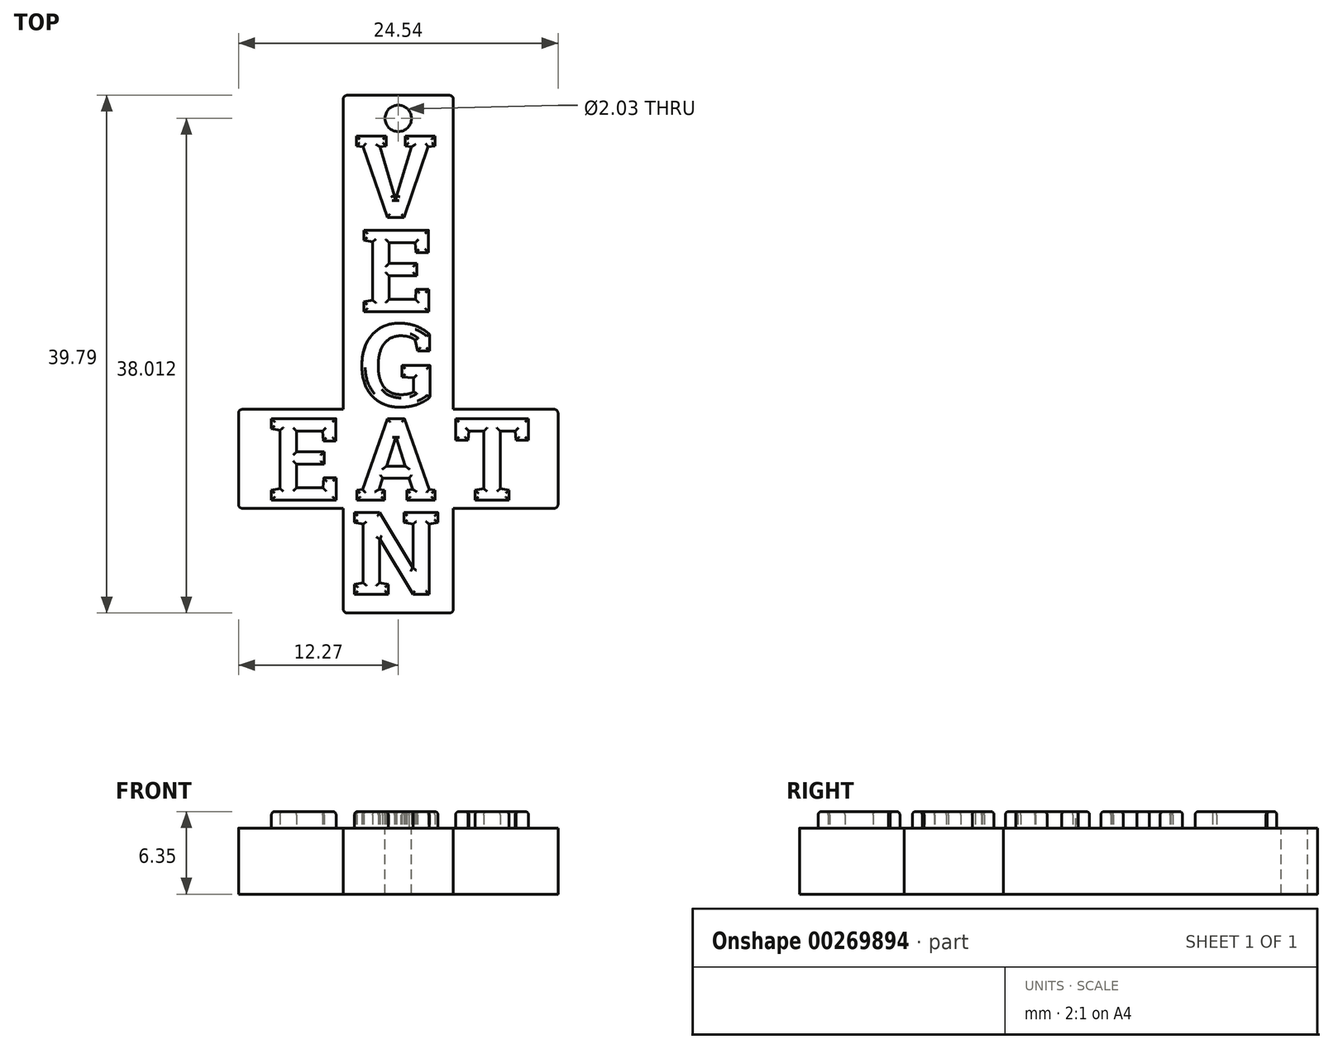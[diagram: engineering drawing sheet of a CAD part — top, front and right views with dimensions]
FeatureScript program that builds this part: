
annotation { "Feature Type Name" : "Feature", "Feature Type Description" : "" }
export const myFeature = defineFeature(function(context is Context, id is Id, definition is map)
    precondition{}
    {
        {
            var Q0;
            Q0=qCreatedBy(makeId("Top.planeOp"),FACE);
            cPlane(context, id + "F0", {"entities" : qUnion([Q0]), "cplaneType" : CPlaneType.OFFSET, "offset" : 5.08 * mm, "width" : 152.4 * mm, "height" : 152.4 * mm});
        }
        {
            var Q0;
            Q0=qCreatedBy(id+"F0.planeOp",FACE);
            var sketch = newSketch(context, id + "F1", { "sketchPlane" : qUnion([Q0])});
            skText(sketch, "E0", { "text": "G", "fontName": "RobotoSlab-Bold.ttf"});
            skText(sketch, "E1", { "text": "E", "fontName": "RobotoSlab-Bold.ttf"});
            skText(sketch, "E2", { "text": "V", "fontName": "RobotoSlab-Bold.ttf"});
            skText(sketch, "E3", { "text": "N", "fontName": "RobotoSlab-Bold.ttf"});
            skText(sketch, "E4", { "text": "A", "fontName": "RobotoSlab-Bold.ttf"});
            skText(sketch, "E5", { "text": "E", "fontName": "RobotoSlab-Bold.ttf"});
            skText(sketch, "E6", { "text": "T", "fontName": "RobotoSlab-Bold.ttf"});
            skPoint(sketch, "E7", {"position": v(-3.35, 0) * mm});
            skPoint(sketch, "E8", {"position": v(3.35, 0) * mm});
            skLineSegment(sketch, "E9", {"start": v(-3.35, 0) * mm, "end": v(3.35, 0) * mm, "construction": true});
            const initialGuessF1  = {"E0": [-0.00299, 0.00406, 1, 0, 0.00635], "E1": [-0.00287, 0.0113, 1, 0, 0.00635], "E2": [-0.00336, 0.01854, 1, 0, 0.00635], "E3": [-0.0036, -0.01041, 1, 0, 0.00635], "E4": [-0.00335, -0.00318, 1, 0, 0.00635], "E5": [-0.00998, -0.00318, 1, 0, 0.00635], "E6": [0.00424, -0.00318, 1, 0, 0.00635]};
            skSetInitialGuess(sketch, initialGuessF1);
            skSolve(sketch);
        }
        {
            var Q0;
            Q0=qCreatedBy(id+"F0.planeOp",FACE);
            var sketch = newSketch(context, id + "F2", { "sketchPlane" : qUnion([Q0])});
            skLineSegment(sketch, "E10.0", {"start": v(-3.6, -10.41) * mm, "end": v(-3.6, -4.06) * mm, "construction": true});
            skLineSegment(sketch, "E10.1", {"start": v(-3.6, -10.41) * mm, "end": v(3.6, -10.41) * mm, "construction": true});
            skLineSegment(sketch, "E10.2", {"start": v(3.6, -10.41) * mm, "end": v(3.6, -4.06) * mm, "construction": true});
            skLineSegment(sketch, "E10.3", {"start": v(-9.98, -3.18) * mm, "end": v(-9.98, 3.17) * mm, "construction": true});
            skLineSegment(sketch, "E10.4", {"start": v(-9.98, -3.18) * mm, "end": v(-4.24, -3.18) * mm, "construction": true});
            skLineSegment(sketch, "E10.5", {"start": v(-9.98, 3.17) * mm, "end": v(-4.24, 3.17) * mm, "construction": true});
            skLineSegment(sketch, "E10.6", {"start": v(4.24, 3.17) * mm, "end": v(10.54, 3.17) * mm, "construction": true});
            skLineSegment(sketch, "E10.7", {"start": v(10.54, -3.18) * mm, "end": v(10.54, 3.17) * mm, "construction": true});
            skLineSegment(sketch, "E10.8", {"start": v(4.24, -3.18) * mm, "end": v(10.54, -3.18) * mm, "construction": true});
            skLineSegment(sketch, "E11.0", {"start": v(-3.36, 18.54) * mm, "end": v(-3.36, 24.9) * mm, "construction": true});
            skLineSegment(sketch, "E11.1", {"start": v(-3.36, 24.9) * mm, "end": v(3.36, 24.9) * mm, "construction": true});
            skLineSegment(sketch, "E11.2", {"start": v(3.36, 18.54) * mm, "end": v(3.36, 24.9) * mm, "construction": true});
            skLineSegment(sketch, "E12.0", {"start": v(-4.23, -11.85) * mm, "end": v(-4.23, -3.81) * mm});
            skLineSegment(sketch, "E13.0", {"start": v(4.23, -11.85) * mm, "end": v(4.23, -3.81) * mm});
            skLineSegment(sketch, "E14.0", {"start": v(-12.27, 3.8) * mm, "end": v(-4.23, 3.8) * mm});
            skLineSegment(sketch, "E15.0", {"start": v(-12.27, -3.81) * mm, "end": v(-4.23, -3.81) * mm});
            skLineSegment(sketch, "E16.0", {"start": v(4.23, 3.8) * mm, "end": v(12.27, 3.8) * mm});
            skLineSegment(sketch, "E17.0", {"start": v(4.23, -3.81) * mm, "end": v(12.27, -3.81) * mm});
            skLineSegment(sketch, "E18.trimOffspring", {"start": v(-4.23, 3.8) * mm, "end": v(-4.23, 27.94) * mm});
            skLineSegment(sketch, "E19.trimOffspring", {"start": v(4.23, 3.8) * mm, "end": v(4.23, 27.94) * mm});
            skLineSegment(sketch, "E20", {"start": v(-12.27, -3.81) * mm, "end": v(-12.27, 3.8) * mm});
            skLineSegment(sketch, "E21", {"start": v(-4.23, -11.85) * mm, "end": v(4.23, -11.85) * mm});
            skLineSegment(sketch, "E22", {"start": v(12.27, -3.81) * mm, "end": v(12.27, 3.8) * mm});
            skLineSegment(sketch, "E23", {"start": v(-4.23, 27.94) * mm, "end": v(4.23, 27.94) * mm});
            skCircle(sketch, "E24", {"center": v(0, 26.16) * mm, "radius": 1.02 * mm});
            skPoint(sketch, "E24.centerSnap0", {"position": v(0, 27.94) * mm});
            skSolve(sketch);
        }
        {
            var Q0;
            Q0 = qSketchRegion(id + "F2", true);
            var Q1;
            Q1=qCreatedBy(makeId("Top.planeOp"),FACE);
            extrude(context, id + "F3", {"entities" : qUnion([Q0]), "endBound" : BoundingType.UP_TO_SURFACE, "oppositeDirection" : true, "endBoundEntityFace" : qUnion([Q1]), "depth" : 25.4 * mm});
        }
        {
            var Q0;
            Q0 = qSketchRegion(id + "F1", true);
            extrude(context, id + "F4", {"entities" : qUnion([Q0]), "depth" : 1.27 * mm});
        }
        {
            var Q0;
            Q0=makeQuery(id+"F3.opExtrude","SWEPT_EDGE",EDGE,{"disambiguationData":[OSD([sQuery(id+"F2.wireOp",EDGE,"E18.trimOffspring"),sQuery(id+"F2.wireOp",EDGE,"E23")])]});
            var Q1;
            Q1=makeQuery(id+"F3.opExtrude","SWEPT_EDGE",EDGE,{"disambiguationData":[OSD([sQuery(id+"F2.wireOp",EDGE,"E19.trimOffspring"),sQuery(id+"F2.wireOp",EDGE,"E23")])]});
            var Q2;
            Q2=makeQuery(id+"F3.opExtrude","SWEPT_EDGE",EDGE,{"disambiguationData":[OSD([sQuery(id+"F2.wireOp",EDGE,"E14.0"),sQuery(id+"F2.wireOp",EDGE,"E20")])]});
            var Q3;
            Q3=makeQuery(id+"F3.opExtrude","SWEPT_EDGE",EDGE,{"disambiguationData":[OSD([sQuery(id+"F2.wireOp",EDGE,"E15.0"),sQuery(id+"F2.wireOp",EDGE,"E20")])]});
            var Q4;
            Q4=makeQuery(id+"F3.opExtrude","SWEPT_EDGE",EDGE,{"disambiguationData":[OSD([sQuery(id+"F2.wireOp",EDGE,"E12.0"),sQuery(id+"F2.wireOp",EDGE,"E21")])]});
            var Q5;
            Q5=makeQuery(id+"F3.opExtrude","SWEPT_EDGE",EDGE,{"disambiguationData":[OSD([sQuery(id+"F2.wireOp",EDGE,"E13.0"),sQuery(id+"F2.wireOp",EDGE,"E21")])]});
            var Q6;
            Q6=makeQuery(id+"F3.opExtrude","SWEPT_EDGE",EDGE,{"disambiguationData":[OSD([sQuery(id+"F2.wireOp",EDGE,"E17.0"),sQuery(id+"F2.wireOp",EDGE,"E22")])]});
            var Q7;
            Q7=makeQuery(id+"F3.opExtrude","SWEPT_EDGE",EDGE,{"disambiguationData":[OSD([sQuery(id+"F2.wireOp",EDGE,"E16.0"),sQuery(id+"F2.wireOp",EDGE,"E22")])]});
            fillet(context, id + "F5", {"entities" : qUnion([Q0, Q1, Q2, Q3, Q4, Q5, Q6, Q7]), "radius" : 0.32 * mm, "tangentPropagation" : true, "allowEdgeOverflow" : false});
        }
        {
            var Q0;
            Q0=makeQuery(id+"F4.opExtrude","CAP_EDGE",EDGE,{"disambiguationData":[OSD([sQuery(id+"F1.wireOp",EDGE,"E2.sketch_text.stroke-13")])],"isStart":false});
            var Q1;
            Q1=makeQuery(id+"F4.opExtrude","CAP_EDGE",EDGE,{"disambiguationData":[OSD([sQuery(id+"F1.wireOp",EDGE,"E2.sketch_text.stroke-12")])],"isStart":false});
            var Q2;
            Q2=makeQuery(id+"F4.opExtrude","CAP_EDGE",EDGE,{"disambiguationData":[OSD([sQuery(id+"F1.wireOp",EDGE,"E2.sketch_text.stroke-11")])],"isStart":false});
            var Q3;
            Q3=makeQuery(id+"F4.opExtrude","CAP_EDGE",EDGE,{"disambiguationData":[OSD([sQuery(id+"F1.wireOp",EDGE,"E2.sketch_text.stroke-1")])],"isStart":false});
            var Q4;
            Q4=makeQuery(id+"F4.opExtrude","CAP_EDGE",EDGE,{"disambiguationData":[OSD([sQuery(id+"F1.wireOp",EDGE,"E2.sketch_text.stroke-5")])],"isStart":false});
            var Q5;
            Q5=makeQuery(id+"F4.opExtrude","CAP_EDGE",EDGE,{"disambiguationData":[OSD([sQuery(id+"F1.wireOp",EDGE,"E2.sketch_text.stroke-4")])],"isStart":false});
            var Q6;
            Q6=makeQuery(id+"F4.opExtrude","CAP_EDGE",EDGE,{"disambiguationData":[OSD([sQuery(id+"F1.wireOp",EDGE,"E2.sketch_text.stroke-2")])],"isStart":false});
            var Q7;
            Q7=makeQuery(id+"F4.opExtrude","CAP_EDGE",EDGE,{"disambiguationData":[OSD([sQuery(id+"F1.wireOp",EDGE,"E2.sketch_text.stroke-14")])],"isStart":false});
            var Q8;
            Q8=makeQuery(id+"F4.opExtrude","CAP_EDGE",EDGE,{"disambiguationData":[OSD([sQuery(id+"F1.wireOp",EDGE,"E2.sketch_text.stroke-15")])],"isStart":false});
            var Q9;
            Q9=makeQuery(id+"F4.opExtrude","CAP_EDGE",EDGE,{"disambiguationData":[OSD([sQuery(id+"F1.wireOp",EDGE,"E2.sketch_text.stroke-16")])],"isStart":false});
            var Q10;
            Q10=makeQuery(id+"F4.opExtrude","CAP_EDGE",EDGE,{"disambiguationData":[OSD([sQuery(id+"F1.wireOp",EDGE,"E2.sketch_text.stroke-17")])],"isStart":false});
            var Q11;
            Q11=makeQuery(id+"F4.opExtrude","CAP_EDGE",EDGE,{"disambiguationData":[OSD([sQuery(id+"F1.wireOp",EDGE,"E2.sketch_text.stroke-0")])],"isStart":false});
            var Q12;
            Q12=makeQuery(id+"F4.opExtrude","CAP_EDGE",EDGE,{"disambiguationData":[OSD([sQuery(id+"F1.wireOp",EDGE,"E2.sketch_text.stroke-7")])],"isStart":false});
            var Q13;
            Q13=makeQuery(id+"F4.opExtrude","CAP_EDGE",EDGE,{"disambiguationData":[OSD([sQuery(id+"F1.wireOp",EDGE,"E2.sketch_text.stroke-6")])],"isStart":false});
            var Q14;
            Q14=makeQuery(id+"F4.opExtrude","CAP_EDGE",EDGE,{"disambiguationData":[OSD([sQuery(id+"F1.wireOp",EDGE,"E2.sketch_text.stroke-8")])],"isStart":false});
            var Q15;
            Q15=makeQuery(id+"F4.opExtrude","CAP_EDGE",EDGE,{"disambiguationData":[OSD([sQuery(id+"F1.wireOp",EDGE,"E2.sketch_text.stroke-10")])],"isStart":false});
            var Q16;
            Q16=makeQuery(id+"F4.opExtrude","CAP_EDGE",EDGE,{"disambiguationData":[OSD([sQuery(id+"F1.wireOp",EDGE,"E2.sketch_text.stroke-9")])],"isStart":false});
            var Q17;
            Q17=makeQuery(id+"F4.opExtrude","CAP_EDGE",EDGE,{"disambiguationData":[OSD([sQuery(id+"F1.wireOp",EDGE,"E1.sketch_text.stroke-9")])],"isStart":false});
            var Q18;
            Q18=makeQuery(id+"F4.opExtrude","CAP_EDGE",EDGE,{"disambiguationData":[OSD([sQuery(id+"F1.wireOp",EDGE,"E1.sketch_text.stroke-8")])],"isStart":false});
            var Q19;
            Q19=makeQuery(id+"F4.opExtrude","CAP_EDGE",EDGE,{"disambiguationData":[OSD([sQuery(id+"F1.wireOp",EDGE,"E1.sketch_text.stroke-7")])],"isStart":false});
            var Q20;
            Q20=makeQuery(id+"F4.opExtrude","CAP_EDGE",EDGE,{"disambiguationData":[OSD([sQuery(id+"F1.wireOp",EDGE,"E1.sketch_text.stroke-6")])],"isStart":false});
            var Q21;
            Q21=makeQuery(id+"F4.opExtrude","CAP_EDGE",EDGE,{"disambiguationData":[OSD([sQuery(id+"F1.wireOp",EDGE,"E1.sketch_text.stroke-5")])],"isStart":false});
            var Q22;
            Q22=makeQuery(id+"F4.opExtrude","CAP_EDGE",EDGE,{"disambiguationData":[OSD([sQuery(id+"F1.wireOp",EDGE,"E1.sketch_text.stroke-4")])],"isStart":false});
            var Q23;
            Q23=makeQuery(id+"F4.opExtrude","CAP_EDGE",EDGE,{"disambiguationData":[OSD([sQuery(id+"F1.wireOp",EDGE,"E1.sketch_text.stroke-3")])],"isStart":false});
            var Q24;
            Q24=makeQuery(id+"F4.opExtrude","CAP_EDGE",EDGE,{"disambiguationData":[OSD([sQuery(id+"F1.wireOp",EDGE,"E1.sketch_text.stroke-2")])],"isStart":false});
            var Q25;
            Q25=makeQuery(id+"F4.opExtrude","CAP_EDGE",EDGE,{"disambiguationData":[OSD([sQuery(id+"F1.wireOp",EDGE,"E1.sketch_text.stroke-1")])],"isStart":false});
            var Q26;
            Q26=makeQuery(id+"F4.opExtrude","CAP_EDGE",EDGE,{"disambiguationData":[OSD([sQuery(id+"F1.wireOp",EDGE,"E1.sketch_text.stroke-0")])],"isStart":false});
            var Q27;
            Q27=makeQuery(id+"F4.opExtrude","CAP_EDGE",EDGE,{"disambiguationData":[OSD([sQuery(id+"F1.wireOp",EDGE,"E1.sketch_text.stroke-20")])],"isStart":false});
            var Q28;
            Q28=makeQuery(id+"F4.opExtrude","CAP_EDGE",EDGE,{"disambiguationData":[OSD([sQuery(id+"F1.wireOp",EDGE,"E1.sketch_text.stroke-19")])],"isStart":false});
            var Q29;
            Q29=makeQuery(id+"F4.opExtrude","CAP_EDGE",EDGE,{"disambiguationData":[OSD([sQuery(id+"F1.wireOp",EDGE,"E1.sketch_text.stroke-18")])],"isStart":false});
            var Q30;
            Q30=makeQuery(id+"F4.opExtrude","CAP_EDGE",EDGE,{"disambiguationData":[OSD([sQuery(id+"F1.wireOp",EDGE,"E1.sketch_text.stroke-17")])],"isStart":false});
            var Q31;
            Q31=makeQuery(id+"F4.opExtrude","CAP_EDGE",EDGE,{"disambiguationData":[OSD([sQuery(id+"F1.wireOp",EDGE,"E1.sketch_text.stroke-16")])],"isStart":false});
            var Q32;
            Q32=makeQuery(id+"F4.opExtrude","CAP_EDGE",EDGE,{"disambiguationData":[OSD([sQuery(id+"F1.wireOp",EDGE,"E1.sketch_text.stroke-15")])],"isStart":false});
            var Q33;
            Q33=makeQuery(id+"F4.opExtrude","CAP_EDGE",EDGE,{"disambiguationData":[OSD([sQuery(id+"F1.wireOp",EDGE,"E1.sketch_text.stroke-14")])],"isStart":false});
            var Q34;
            Q34=makeQuery(id+"F4.opExtrude","CAP_EDGE",EDGE,{"disambiguationData":[OSD([sQuery(id+"F1.wireOp",EDGE,"E1.sketch_text.stroke-12"),sQuery(id+"F1.wireOp",EDGE,"E1.sketch_text.stroke-13")])],"isStart":false});
            var Q35;
            Q35=makeQuery(id+"F4.opExtrude","CAP_EDGE",EDGE,{"disambiguationData":[OSD([sQuery(id+"F1.wireOp",EDGE,"E1.sketch_text.stroke-11")])],"isStart":false});
            var Q36;
            Q36=makeQuery(id+"F4.opExtrude","CAP_EDGE",EDGE,{"disambiguationData":[OSD([sQuery(id+"F1.wireOp",EDGE,"E1.sketch_text.stroke-10")])],"isStart":false});
            var Q37;
            Q37=makeQuery(id+"F4.opExtrude","CAP_EDGE",EDGE,{"disambiguationData":[OSD([sQuery(id+"F1.wireOp",EDGE,"E0.sketch_text.stroke-3")])],"isStart":false});
            var Q38;
            Q38=makeQuery(id+"F4.opExtrude","CAP_EDGE",EDGE,{"disambiguationData":[OSD([sQuery(id+"F1.wireOp",EDGE,"E0.sketch_text.stroke-9")])],"isStart":false});
            var Q39;
            Q39=makeQuery(id+"F4.opExtrude","CAP_EDGE",EDGE,{"disambiguationData":[OSD([sQuery(id+"F1.wireOp",EDGE,"E0.sketch_text.stroke-10")])],"isStart":false});
            var Q40;
            Q40=makeQuery(id+"F4.opExtrude","CAP_EDGE",EDGE,{"disambiguationData":[OSD([sQuery(id+"F1.wireOp",EDGE,"E0.sketch_text.stroke-11")])],"isStart":false});
            var Q41;
            Q41=makeQuery(id+"F4.opExtrude","CAP_EDGE",EDGE,{"disambiguationData":[OSD([sQuery(id+"F1.wireOp",EDGE,"E0.sketch_text.stroke-12")])],"isStart":false});
            var Q42;
            Q42=makeQuery(id+"F4.opExtrude","CAP_EDGE",EDGE,{"disambiguationData":[OSD([sQuery(id+"F1.wireOp",EDGE,"E0.sketch_text.stroke-21")])],"isStart":false});
            var Q43;
            Q43=makeQuery(id+"F4.opExtrude","CAP_EDGE",EDGE,{"disambiguationData":[OSD([sQuery(id+"F1.wireOp",EDGE,"E0.sketch_text.stroke-25")])],"isStart":false});
            var Q44;
            Q44=makeQuery(id+"F4.opExtrude","CAP_EDGE",EDGE,{"disambiguationData":[OSD([sQuery(id+"F1.wireOp",EDGE,"E0.sketch_text.stroke-24")])],"isStart":false});
            var Q45;
            Q45=makeQuery(id+"F4.opExtrude","CAP_EDGE",EDGE,{"disambiguationData":[OSD([sQuery(id+"F1.wireOp",EDGE,"E0.sketch_text.stroke-23")])],"isStart":false});
            var Q46;
            Q46=makeQuery(id+"F4.opExtrude","CAP_EDGE",EDGE,{"disambiguationData":[OSD([sQuery(id+"F1.wireOp",EDGE,"E0.sketch_text.stroke-22")])],"isStart":false});
            var Q47;
            Q47=makeQuery(id+"F4.opExtrude","CAP_EDGE",EDGE,{"disambiguationData":[OSD([sQuery(id+"F1.wireOp",EDGE,"E4.sketch_text.stroke-1")])],"isStart":false});
            var Q48;
            Q48=makeQuery(id+"F4.opExtrude","CAP_EDGE",EDGE,{"disambiguationData":[OSD([sQuery(id+"F1.wireOp",EDGE,"E4.sketch_text.stroke-2")])],"isStart":false});
            var Q49;
            Q49=makeQuery(id+"F4.opExtrude","CAP_EDGE",EDGE,{"disambiguationData":[OSD([sQuery(id+"F1.wireOp",EDGE,"E4.sketch_text.stroke-3")])],"isStart":false});
            var Q50;
            Q50=makeQuery(id+"F4.opExtrude","CAP_EDGE",EDGE,{"disambiguationData":[OSD([sQuery(id+"F1.wireOp",EDGE,"E4.sketch_text.stroke-16")])],"isStart":false});
            var Q51;
            Q51=makeQuery(id+"F4.opExtrude","CAP_EDGE",EDGE,{"disambiguationData":[OSD([sQuery(id+"F1.wireOp",EDGE,"E4.sketch_text.stroke-19")])],"isStart":false});
            var Q52;
            Q52=makeQuery(id+"F4.opExtrude","CAP_EDGE",EDGE,{"disambiguationData":[OSD([sQuery(id+"F1.wireOp",EDGE,"E4.sketch_text.stroke-17")])],"isStart":false});
            var Q53;
            Q53=makeQuery(id+"F4.opExtrude","CAP_EDGE",EDGE,{"disambiguationData":[OSD([sQuery(id+"F1.wireOp",EDGE,"E4.sketch_text.stroke-10")])],"isStart":false});
            var Q54;
            Q54=makeQuery(id+"F4.opExtrude","CAP_EDGE",EDGE,{"disambiguationData":[OSD([sQuery(id+"F1.wireOp",EDGE,"E4.sketch_text.stroke-11")])],"isStart":false});
            var Q55;
            Q55=makeQuery(id+"F4.opExtrude","CAP_EDGE",EDGE,{"disambiguationData":[OSD([sQuery(id+"F1.wireOp",EDGE,"E4.sketch_text.stroke-9")])],"isStart":false});
            var Q56;
            Q56=makeQuery(id+"F4.opExtrude","CAP_EDGE",EDGE,{"disambiguationData":[OSD([sQuery(id+"F1.wireOp",EDGE,"E4.sketch_text.stroke-8")])],"isStart":false});
            var Q57;
            Q57=makeQuery(id+"F4.opExtrude","CAP_EDGE",EDGE,{"disambiguationData":[OSD([sQuery(id+"F1.wireOp",EDGE,"E4.sketch_text.stroke-7")])],"isStart":false});
            var Q58;
            Q58=makeQuery(id+"F4.opExtrude","CAP_EDGE",EDGE,{"disambiguationData":[OSD([sQuery(id+"F1.wireOp",EDGE,"E4.sketch_text.stroke-4")])],"isStart":false});
            var Q59;
            Q59=makeQuery(id+"F4.opExtrude","CAP_EDGE",EDGE,{"disambiguationData":[OSD([sQuery(id+"F1.wireOp",EDGE,"E4.sketch_text.stroke-5")])],"isStart":false});
            var Q60;
            Q60=makeQuery(id+"F4.opExtrude","CAP_EDGE",EDGE,{"disambiguationData":[OSD([sQuery(id+"F1.wireOp",EDGE,"E4.sketch_text.stroke-6")])],"isStart":false});
            var Q61;
            Q61=makeQuery(id+"F4.opExtrude","CAP_EDGE",EDGE,{"disambiguationData":[OSD([sQuery(id+"F1.wireOp",EDGE,"E4.sketch_text.stroke-13")])],"isStart":false});
            var Q62;
            Q62=makeQuery(id+"F4.opExtrude","CAP_EDGE",EDGE,{"disambiguationData":[OSD([sQuery(id+"F1.wireOp",EDGE,"E4.sketch_text.stroke-12")])],"isStart":false});
            var Q63;
            Q63=makeQuery(id+"F4.opExtrude","CAP_EDGE",EDGE,{"disambiguationData":[OSD([sQuery(id+"F1.wireOp",EDGE,"E4.sketch_text.stroke-0")])],"isStart":false});
            var Q64;
            Q64=makeQuery(id+"F4.opExtrude","CAP_EDGE",EDGE,{"disambiguationData":[OSD([sQuery(id+"F1.wireOp",EDGE,"E4.sketch_text.stroke-15")])],"isStart":false});
            var Q65;
            Q65=makeQuery(id+"F4.opExtrude","CAP_EDGE",EDGE,{"disambiguationData":[OSD([sQuery(id+"F1.wireOp",EDGE,"E4.sketch_text.stroke-14")])],"isStart":false});
            var Q66;
            Q66=makeQuery(id+"F4.opExtrude","CAP_EDGE",EDGE,{"disambiguationData":[OSD([sQuery(id+"F1.wireOp",EDGE,"E5.sketch_text.stroke-9")])],"isStart":false});
            var Q67;
            Q67=makeQuery(id+"F4.opExtrude","CAP_EDGE",EDGE,{"disambiguationData":[OSD([sQuery(id+"F1.wireOp",EDGE,"E5.sketch_text.stroke-8")])],"isStart":false});
            var Q68;
            Q68=makeQuery(id+"F4.opExtrude","CAP_EDGE",EDGE,{"disambiguationData":[OSD([sQuery(id+"F1.wireOp",EDGE,"E5.sketch_text.stroke-7")])],"isStart":false});
            var Q69;
            Q69=makeQuery(id+"F4.opExtrude","CAP_EDGE",EDGE,{"disambiguationData":[OSD([sQuery(id+"F1.wireOp",EDGE,"E5.sketch_text.stroke-6")])],"isStart":false});
            var Q70;
            Q70=makeQuery(id+"F4.opExtrude","CAP_EDGE",EDGE,{"disambiguationData":[OSD([sQuery(id+"F1.wireOp",EDGE,"E5.sketch_text.stroke-5")])],"isStart":false});
            var Q71;
            Q71=makeQuery(id+"F4.opExtrude","CAP_EDGE",EDGE,{"disambiguationData":[OSD([sQuery(id+"F1.wireOp",EDGE,"E5.sketch_text.stroke-4")])],"isStart":false});
            var Q72;
            Q72=makeQuery(id+"F4.opExtrude","CAP_EDGE",EDGE,{"disambiguationData":[OSD([sQuery(id+"F1.wireOp",EDGE,"E5.sketch_text.stroke-3")])],"isStart":false});
            var Q73;
            Q73=makeQuery(id+"F4.opExtrude","CAP_EDGE",EDGE,{"disambiguationData":[OSD([sQuery(id+"F1.wireOp",EDGE,"E5.sketch_text.stroke-2")])],"isStart":false});
            var Q74;
            Q74=makeQuery(id+"F4.opExtrude","CAP_EDGE",EDGE,{"disambiguationData":[OSD([sQuery(id+"F1.wireOp",EDGE,"E5.sketch_text.stroke-1")])],"isStart":false});
            var Q75;
            Q75=makeQuery(id+"F4.opExtrude","CAP_EDGE",EDGE,{"disambiguationData":[OSD([sQuery(id+"F1.wireOp",EDGE,"E5.sketch_text.stroke-0")])],"isStart":false});
            var Q76;
            Q76=makeQuery(id+"F4.opExtrude","CAP_EDGE",EDGE,{"disambiguationData":[OSD([sQuery(id+"F1.wireOp",EDGE,"E5.sketch_text.stroke-20")])],"isStart":false});
            var Q77;
            Q77=makeQuery(id+"F4.opExtrude","CAP_EDGE",EDGE,{"disambiguationData":[OSD([sQuery(id+"F1.wireOp",EDGE,"E5.sketch_text.stroke-19")])],"isStart":false});
            var Q78;
            Q78=makeQuery(id+"F4.opExtrude","CAP_EDGE",EDGE,{"disambiguationData":[OSD([sQuery(id+"F1.wireOp",EDGE,"E5.sketch_text.stroke-18")])],"isStart":false});
            var Q79;
            Q79=makeQuery(id+"F4.opExtrude","CAP_EDGE",EDGE,{"disambiguationData":[OSD([sQuery(id+"F1.wireOp",EDGE,"E5.sketch_text.stroke-17")])],"isStart":false});
            var Q80;
            Q80=makeQuery(id+"F4.opExtrude","CAP_EDGE",EDGE,{"disambiguationData":[OSD([sQuery(id+"F1.wireOp",EDGE,"E5.sketch_text.stroke-16")])],"isStart":false});
            var Q81;
            Q81=makeQuery(id+"F4.opExtrude","CAP_EDGE",EDGE,{"disambiguationData":[OSD([sQuery(id+"F1.wireOp",EDGE,"E5.sketch_text.stroke-15")])],"isStart":false});
            var Q82;
            Q82=makeQuery(id+"F4.opExtrude","CAP_EDGE",EDGE,{"disambiguationData":[OSD([sQuery(id+"F1.wireOp",EDGE,"E5.sketch_text.stroke-14")])],"isStart":false});
            var Q83;
            Q83=makeQuery(id+"F4.opExtrude","CAP_EDGE",EDGE,{"disambiguationData":[OSD([sQuery(id+"F1.wireOp",EDGE,"E5.sketch_text.stroke-12"),sQuery(id+"F1.wireOp",EDGE,"E5.sketch_text.stroke-13")])],"isStart":false});
            var Q84;
            Q84=makeQuery(id+"F4.opExtrude","CAP_EDGE",EDGE,{"disambiguationData":[OSD([sQuery(id+"F1.wireOp",EDGE,"E5.sketch_text.stroke-11")])],"isStart":false});
            var Q85;
            Q85=makeQuery(id+"F4.opExtrude","CAP_EDGE",EDGE,{"disambiguationData":[OSD([sQuery(id+"F1.wireOp",EDGE,"E5.sketch_text.stroke-10")])],"isStart":false});
            var Q86;
            Q86=makeQuery(id+"F4.opExtrude","CAP_EDGE",EDGE,{"disambiguationData":[OSD([sQuery(id+"F1.wireOp",EDGE,"E6.sketch_text.stroke-10")])],"isStart":false});
            var Q87;
            Q87=makeQuery(id+"F4.opExtrude","CAP_EDGE",EDGE,{"disambiguationData":[OSD([sQuery(id+"F1.wireOp",EDGE,"E6.sketch_text.stroke-4")])],"isStart":false});
            var Q88;
            Q88=makeQuery(id+"F4.opExtrude","CAP_EDGE",EDGE,{"disambiguationData":[OSD([sQuery(id+"F1.wireOp",EDGE,"E6.sketch_text.stroke-9")])],"isStart":false});
            var Q89;
            Q89=makeQuery(id+"F4.opExtrude","CAP_EDGE",EDGE,{"disambiguationData":[OSD([sQuery(id+"F1.wireOp",EDGE,"E6.sketch_text.stroke-8")])],"isStart":false});
            var Q90;
            Q90=makeQuery(id+"F4.opExtrude","CAP_EDGE",EDGE,{"disambiguationData":[OSD([sQuery(id+"F1.wireOp",EDGE,"E6.sketch_text.stroke-7")])],"isStart":false});
            var Q91;
            Q91=makeQuery(id+"F4.opExtrude","CAP_EDGE",EDGE,{"disambiguationData":[OSD([sQuery(id+"F1.wireOp",EDGE,"E6.sketch_text.stroke-6")])],"isStart":false});
            var Q92;
            Q92=makeQuery(id+"F4.opExtrude","CAP_EDGE",EDGE,{"disambiguationData":[OSD([sQuery(id+"F1.wireOp",EDGE,"E6.sketch_text.stroke-5")])],"isStart":false});
            var Q93;
            Q93=makeQuery(id+"F4.opExtrude","CAP_EDGE",EDGE,{"disambiguationData":[OSD([sQuery(id+"F1.wireOp",EDGE,"E6.sketch_text.stroke-11")])],"isStart":false});
            var Q94;
            Q94=makeQuery(id+"F4.opExtrude","CAP_EDGE",EDGE,{"disambiguationData":[OSD([sQuery(id+"F1.wireOp",EDGE,"E6.sketch_text.stroke-12")])],"isStart":false});
            var Q95;
            Q95=makeQuery(id+"F4.opExtrude","CAP_EDGE",EDGE,{"disambiguationData":[OSD([sQuery(id+"F1.wireOp",EDGE,"E6.sketch_text.stroke-13")])],"isStart":false});
            var Q96;
            Q96=makeQuery(id+"F4.opExtrude","CAP_EDGE",EDGE,{"disambiguationData":[OSD([sQuery(id+"F1.wireOp",EDGE,"E6.sketch_text.stroke-14")])],"isStart":false});
            var Q97;
            Q97=makeQuery(id+"F4.opExtrude","CAP_EDGE",EDGE,{"disambiguationData":[OSD([sQuery(id+"F1.wireOp",EDGE,"E6.sketch_text.stroke-15")])],"isStart":false});
            var Q98;
            Q98=makeQuery(id+"F4.opExtrude","CAP_EDGE",EDGE,{"disambiguationData":[OSD([sQuery(id+"F1.wireOp",EDGE,"E6.sketch_text.stroke-0")])],"isStart":false});
            var Q99;
            Q99=makeQuery(id+"F4.opExtrude","CAP_EDGE",EDGE,{"disambiguationData":[OSD([sQuery(id+"F1.wireOp",EDGE,"E6.sketch_text.stroke-1")])],"isStart":false});
            var Q100;
            Q100=makeQuery(id+"F4.opExtrude","CAP_EDGE",EDGE,{"disambiguationData":[OSD([sQuery(id+"F1.wireOp",EDGE,"E6.sketch_text.stroke-2")])],"isStart":false});
            var Q101;
            Q101=makeQuery(id+"F4.opExtrude","CAP_EDGE",EDGE,{"disambiguationData":[OSD([sQuery(id+"F1.wireOp",EDGE,"E6.sketch_text.stroke-3")])],"isStart":false});
            var Q102;
            Q102=makeQuery(id+"F4.opExtrude","CAP_EDGE",EDGE,{"disambiguationData":[OSD([sQuery(id+"F1.wireOp",EDGE,"E3.sketch_text.stroke-12")])],"isStart":false});
            var Q103;
            Q103=makeQuery(id+"F4.opExtrude","CAP_EDGE",EDGE,{"disambiguationData":[OSD([sQuery(id+"F1.wireOp",EDGE,"E3.sketch_text.stroke-13")])],"isStart":false});
            var Q104;
            Q104=makeQuery(id+"F4.opExtrude","CAP_EDGE",EDGE,{"disambiguationData":[OSD([sQuery(id+"F1.wireOp",EDGE,"E3.sketch_text.stroke-14")])],"isStart":false});
            var Q105;
            Q105=makeQuery(id+"F4.opExtrude","CAP_EDGE",EDGE,{"disambiguationData":[OSD([sQuery(id+"F1.wireOp",EDGE,"E3.sketch_text.stroke-15"),sQuery(id+"F1.wireOp",EDGE,"E3.sketch_text.stroke-16")])],"isStart":false});
            var Q106;
            Q106=makeQuery(id+"F4.opExtrude","CAP_EDGE",EDGE,{"disambiguationData":[OSD([sQuery(id+"F1.wireOp",EDGE,"E3.sketch_text.stroke-17")])],"isStart":false});
            var Q107;
            Q107=makeQuery(id+"F4.opExtrude","CAP_EDGE",EDGE,{"disambiguationData":[OSD([sQuery(id+"F1.wireOp",EDGE,"E3.sketch_text.stroke-19")])],"isStart":false});
            var Q108;
            Q108=makeQuery(id+"F4.opExtrude","CAP_EDGE",EDGE,{"disambiguationData":[OSD([sQuery(id+"F1.wireOp",EDGE,"E3.sketch_text.stroke-20")])],"isStart":false});
            var Q109;
            Q109=makeQuery(id+"F4.opExtrude","CAP_EDGE",EDGE,{"disambiguationData":[OSD([sQuery(id+"F1.wireOp",EDGE,"E3.sketch_text.stroke-21")])],"isStart":false});
            var Q110;
            Q110=makeQuery(id+"F4.opExtrude","CAP_EDGE",EDGE,{"disambiguationData":[OSD([sQuery(id+"F1.wireOp",EDGE,"E3.sketch_text.stroke-22"),sQuery(id+"F1.wireOp",EDGE,"E3.sketch_text.stroke-23")])],"isStart":false});
            var Q111;
            Q111=makeQuery(id+"F4.opExtrude","CAP_EDGE",EDGE,{"disambiguationData":[OSD([sQuery(id+"F1.wireOp",EDGE,"E3.sketch_text.stroke-0")])],"isStart":false});
            var Q112;
            Q112=makeQuery(id+"F4.opExtrude","CAP_EDGE",EDGE,{"disambiguationData":[OSD([sQuery(id+"F1.wireOp",EDGE,"E3.sketch_text.stroke-1")])],"isStart":false});
            var Q113;
            Q113=makeQuery(id+"F4.opExtrude","CAP_EDGE",EDGE,{"disambiguationData":[OSD([sQuery(id+"F1.wireOp",EDGE,"E3.sketch_text.stroke-2")])],"isStart":false});
            var Q114;
            Q114=makeQuery(id+"F4.opExtrude","CAP_EDGE",EDGE,{"disambiguationData":[OSD([sQuery(id+"F1.wireOp",EDGE,"E3.sketch_text.stroke-3")])],"isStart":false});
            var Q115;
            Q115=makeQuery(id+"F4.opExtrude","CAP_EDGE",EDGE,{"disambiguationData":[OSD([sQuery(id+"F1.wireOp",EDGE,"E3.sketch_text.stroke-4")])],"isStart":false});
            var Q116;
            Q116=makeQuery(id+"F4.opExtrude","CAP_EDGE",EDGE,{"disambiguationData":[OSD([sQuery(id+"F1.wireOp",EDGE,"E3.sketch_text.stroke-6")])],"isStart":false});
            var Q117;
            Q117=makeQuery(id+"F4.opExtrude","CAP_EDGE",EDGE,{"disambiguationData":[OSD([sQuery(id+"F1.wireOp",EDGE,"E3.sketch_text.stroke-7")])],"isStart":false});
            var Q118;
            Q118=makeQuery(id+"F4.opExtrude","CAP_EDGE",EDGE,{"disambiguationData":[OSD([sQuery(id+"F1.wireOp",EDGE,"E3.sketch_text.stroke-8")])],"isStart":false});
            var Q119;
            Q119=makeQuery(id+"F4.opExtrude","CAP_FACE",FACE,{"disambiguationData":[OSD([sQuery(id+"F1.wireOp",EDGE,"E3.sketch_text.stroke-0"),sQuery(id+"F1.wireOp",EDGE,"E3.sketch_text.stroke-1"),sQuery(id+"F1.wireOp",EDGE,"E3.sketch_text.stroke-2"),sQuery(id+"F1.wireOp",EDGE,"E3.sketch_text.stroke-3"),sQuery(id+"F1.wireOp",EDGE,"E3.sketch_text.stroke-4"),sQuery(id+"F1.wireOp",EDGE,"E3.sketch_text.stroke-5"),sQuery(id+"F1.wireOp",EDGE,"E3.sketch_text.stroke-6"),sQuery(id+"F1.wireOp",EDGE,"E3.sketch_text.stroke-7"),sQuery(id+"F1.wireOp",EDGE,"E3.sketch_text.stroke-8"),sQuery(id+"F1.wireOp",EDGE,"E3.sketch_text.stroke-9"),sQuery(id+"F1.wireOp",EDGE,"E3.sketch_text.stroke-10"),sQuery(id+"F1.wireOp",EDGE,"E3.sketch_text.stroke-11"),sQuery(id+"F1.wireOp",EDGE,"E3.sketch_text.stroke-12"),sQuery(id+"F1.wireOp",EDGE,"E3.sketch_text.stroke-13"),sQuery(id+"F1.wireOp",EDGE,"E3.sketch_text.stroke-14"),sQuery(id+"F1.wireOp",EDGE,"E3.sketch_text.stroke-15"),sQuery(id+"F1.wireOp",EDGE,"E3.sketch_text.stroke-16"),sQuery(id+"F1.wireOp",EDGE,"E3.sketch_text.stroke-17"),sQuery(id+"F1.wireOp",EDGE,"E3.sketch_text.stroke-18"),sQuery(id+"F1.wireOp",EDGE,"E3.sketch_text.stroke-19"),sQuery(id+"F1.wireOp",EDGE,"E3.sketch_text.stroke-20"),sQuery(id+"F1.wireOp",EDGE,"E3.sketch_text.stroke-21"),sQuery(id+"F1.wireOp",EDGE,"E3.sketch_text.stroke-22"),sQuery(id+"F1.wireOp",EDGE,"E3.sketch_text.stroke-23")])],"isStart":false});
            fillet(context, id + "F6", {"entities" : qUnion([Q0, Q1, Q2, Q3, Q4, Q5, Q6, Q7, Q8, Q9, Q10, Q11, Q12, Q13, Q14, Q15, Q16, Q17, Q18, Q19, Q20, Q21, Q22, Q23, Q24, Q25, Q26, Q27, Q28, Q29, Q30, Q31, Q32, Q33, Q34, Q35, Q36, Q37, Q38, Q39, Q40, Q41, Q42, Q43, Q44, Q45, Q46, Q47, Q48, Q49, Q50, Q51, Q52, Q53, Q54, Q55, Q56, Q57, Q58, Q59, Q60, Q61, Q62, Q63, Q64, Q65, Q66, Q67, Q68, Q69, Q70, Q71, Q72, Q73, Q74, Q75, Q76, Q77, Q78, Q79, Q80, Q81, Q82, Q83, Q84, Q85, Q86, Q87, Q88, Q89, Q90, Q91, Q92, Q93, Q94, Q95, Q96, Q97, Q98, Q99, Q100, Q101, Q102, Q103, Q104, Q105, Q106, Q107, Q108, Q109, Q110, Q111, Q112, Q113, Q114, Q115, Q116, Q117, Q118, Q119]), "radius" : 0.25 * mm, "tangentPropagation" : true, "allowEdgeOverflow" : false});
        }
    });
